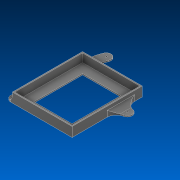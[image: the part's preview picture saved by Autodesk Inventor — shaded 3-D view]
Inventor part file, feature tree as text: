
AUTODESK INVENTOR PART (.ipt)
format: ipt  version: 2022.2 (Build 262287000, 287)  size: 180,224 bytes
history: native  units: in
note: dims shown in document units (in); Inventor stores cm internally (conversion verified against a paired STEP export)
features: extrude x3, sketch x3, fillet x1, hole x1, projected_geometry x1
ambient origin geometry x8: Origin, YZ Plane, XZ Plane, XY Plane, X Axis, Y Axis, Z Axis, Center Point
bodies: Solid1 (feature_tree)
feature tree (9):
  extrude  "Extrusion1"  Depth=1.0in
  extrude  "Extrusion2"  Depth=7.1in
  sketch  "Sketch4"  dims[d4=0.125in d5=0.0in d6=0.125in d7=1.0in d8=0.0in d9=1.0in d10=0.175in d11=0.6859in d12=1.65in d14=5.1109in d15=0.5in d16=0.125in d17=0.0in d18=0.175in d19=0.75in d20=0.35in d21=0.0in d22=0.5635in d23=1.0in d24=0.8108in d26=0.825in d27=0.5in]
  extrude  "Extrusion3"  Depth=0.5in
  fillet  "Fillet1"  Radius=1.0in
  hole  "Hole1"  [1 undecoded]
  sketch  "Sketch1"  dims[d0=1.0in d1=1.0in]
  sketch  "Sketch3"  dims[d2=6.0in d3=7.1in]
  projected_geometry  "Projected Loop1"
note: 1 required parameter value undecoded (feature->parameter linkage not recoverable at this tier; creation-order binding heuristic only, values carry confidence <= 0.55)
